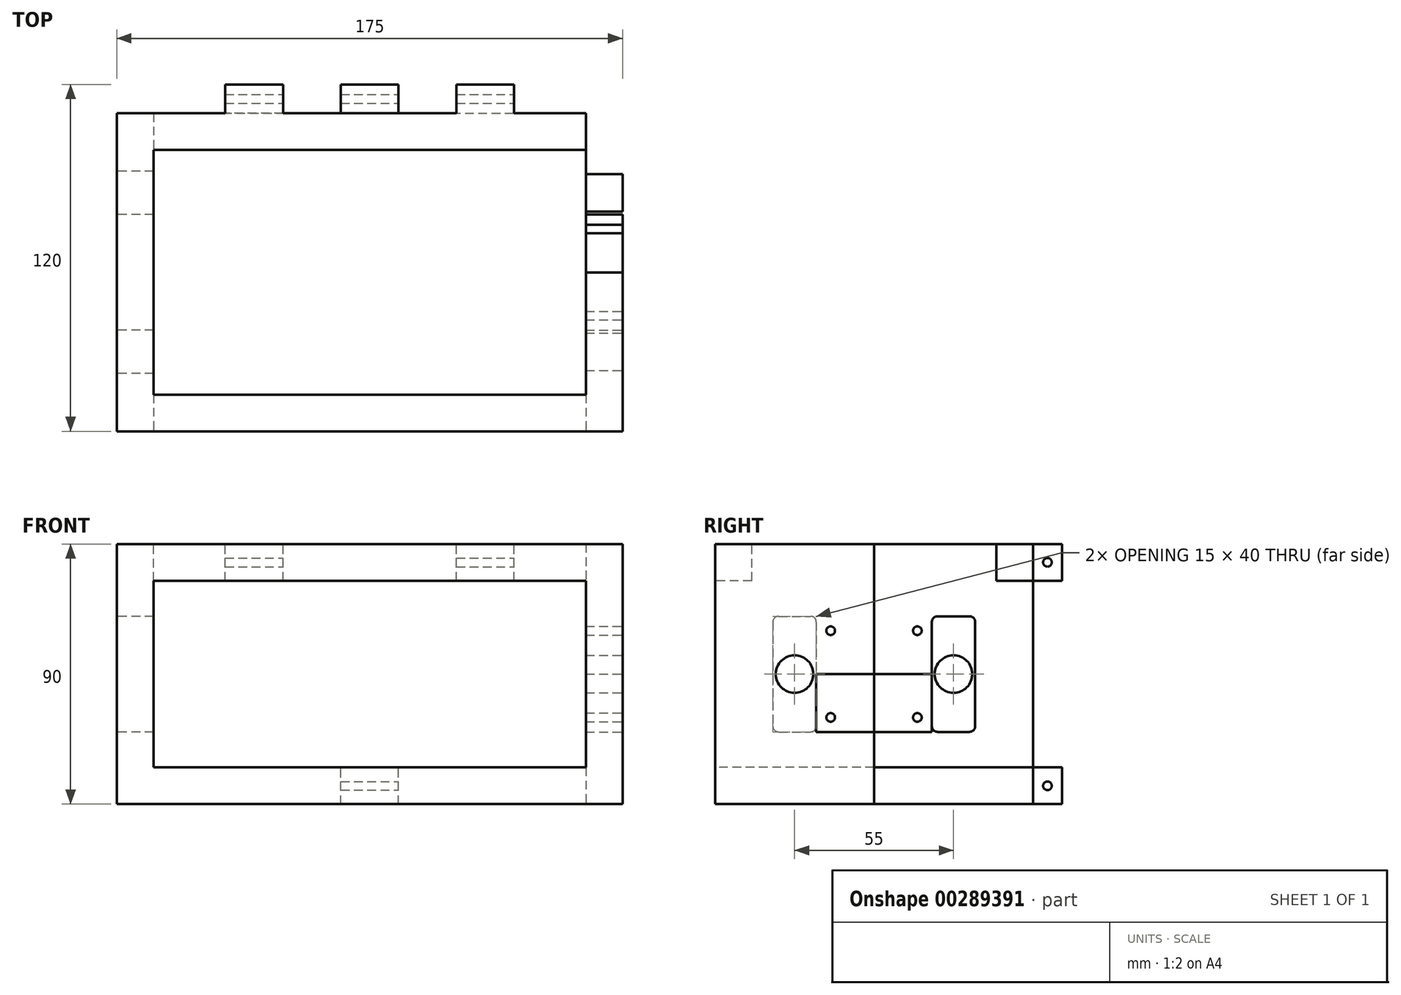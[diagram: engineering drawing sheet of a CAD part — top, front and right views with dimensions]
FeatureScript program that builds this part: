
annotation { "Feature Type Name" : "Feature", "Feature Type Description" : "" }
export const myFeature = defineFeature(function(context is Context, id is Id, definition is map)
    precondition{}
    {
        {
            var Q0;
            Q0=qCreatedBy(makeId("Front.planeOp"),FACE);
            var sketch = newSketch(context, id + "F0", { "sketchPlane" : qUnion([Q0])});
            skLineSegment(sketch, "E0.bottom", {"start": v(-87.5, 45) * mm, "end": v(87.5, 45) * mm});
            skLineSegment(sketch, "E0.top", {"start": v(-87.5, -45) * mm, "end": v(87.5, -45) * mm});
            skLineSegment(sketch, "E0.left", {"start": v(-87.5, 45) * mm, "end": v(-87.5, -45) * mm});
            skLineSegment(sketch, "E0.right", {"start": v(87.5, 45) * mm, "end": v(87.5, -45) * mm});
            skPoint(sketch, "E0.middle", {"position": v(0, 0) * mm});
            skSolve(sketch);
        }
        {
            var Q0;
            Q0 = qSketchRegion(id + "F0", true);
            extrude(context, id + "F1", {"entities" : qUnion([Q0]), "endBound" : BoundingType.SYMMETRIC, "depth" : 110 * mm});
        }
        {
            var Q0;
            Q0=makeQuery(id+"F1.opExtrude","SWEPT_FACE",FACE,{"disambiguationData":[OSD([sQuery(id+"F0.wireOp",EDGE,"E0.left")])]});
            var sketch = newSketch(context, id + "F2", { "sketchPlane" : qUnion([Q0])});
            skLineSegment(sketch, "E1", {"start": v(0, 45) * mm, "end": v(0, 10) * mm});
            skLineSegment(sketch, "E2", {"start": v(-55, 0) * mm, "end": v(-35, 0) * mm});
            skLineSegment(sketch, "E3.bottom", {"start": v(-33, 20) * mm, "end": v(-22, 20) * mm});
            skLineSegment(sketch, "E3.top", {"start": v(-33, -20) * mm, "end": v(-22, -20) * mm});
            skLineSegment(sketch, "E3.left", {"start": v(-35, 18) * mm, "end": v(-35, -18) * mm});
            skLineSegment(sketch, "E3.right", {"start": v(-20, 18) * mm, "end": v(-20, -18) * mm});
            skPoint(sketch, "E3.middle", {"position": v(-27.5, 0) * mm});
            skLineSegment(sketch, "E4.MirrorCS", {"start": v(20, 18) * mm, "end": v(20, -18) * mm});
            skLineSegment(sketch, "E5.MirrorCS", {"start": v(33, 20) * mm, "end": v(22, 20) * mm});
            skLineSegment(sketch, "E6.MirrorCS", {"start": v(35, 18) * mm, "end": v(35, -18) * mm});
            skLineSegment(sketch, "E7.MirrorCS", {"start": v(33, -20) * mm, "end": v(22, -20) * mm});
            skPoint(sketch, "E8.visualSharp", {"position": v(-35, 20) * mm});
            skArc(sketch, "E8.filletArc", {"start": v(-33, 20) * mm, "mid": v(-34.41, 19.41) * mm, "end": v(-35, 18) * mm});
            skPoint(sketch, "E9.visualSharp", {"position": v(-20, 20) * mm});
            skArc(sketch, "E9.filletArc", {"start": v(-20, 18) * mm, "mid": v(-20.59, 19.41) * mm, "end": v(-22, 20) * mm});
            skPoint(sketch, "E10.visualSharp", {"position": v(-35, -20) * mm});
            skArc(sketch, "E10.filletArc", {"start": v(-35, -18) * mm, "mid": v(-34.41, -19.41) * mm, "end": v(-33, -20) * mm});
            skPoint(sketch, "E11.visualSharp", {"position": v(-20, -20) * mm});
            skArc(sketch, "E11.filletArc", {"start": v(-22, -20) * mm, "mid": v(-20.59, -19.41) * mm, "end": v(-20, -18) * mm});
            skPoint(sketch, "E12.visualSharp", {"position": v(20, 20) * mm});
            skArc(sketch, "E12.filletArc", {"start": v(22, 20) * mm, "mid": v(20.59, 19.41) * mm, "end": v(20, 18) * mm});
            skPoint(sketch, "E13.visualSharp", {"position": v(35, 20) * mm});
            skArc(sketch, "E13.filletArc", {"start": v(35, 18) * mm, "mid": v(34.41, 19.41) * mm, "end": v(33, 20) * mm});
            skPoint(sketch, "E14.visualSharp", {"position": v(20, -20) * mm});
            skArc(sketch, "E14.filletArc", {"start": v(20, -18) * mm, "mid": v(20.59, -19.41) * mm, "end": v(22, -20) * mm});
            skPoint(sketch, "E15.visualSharp", {"position": v(35, -20) * mm});
            skArc(sketch, "E15.filletArc", {"start": v(33, -20) * mm, "mid": v(34.41, -19.41) * mm, "end": v(35, -18) * mm});
            skLineSegment(sketch, "E16.trimOffspring", {"start": v(-20, 0) * mm, "end": v(-2.5, 0) * mm});
            skLineSegment(sketch, "E17.trimOffspring", {"start": v(2.5, 0) * mm, "end": v(20, 0) * mm});
            skLineSegment(sketch, "E18.trimOffspring", {"start": v(0, -10) * mm, "end": v(0, -45) * mm});
            skLineSegment(sketch, "E19.trimOffspring", {"start": v(35, 0) * mm, "end": v(55, 0) * mm});
            skLineSegment(sketch, "E20", {"start": v(0, 10) * mm, "end": v(0, -10) * mm});
            skLineSegment(sketch, "E21", {"start": v(2.5, 0) * mm, "end": v(-2.5, 0) * mm});
            skSolve(sketch);
        }
        {
            var Q0;
            Q0=makeQuery(id+"F1.opExtrude","CAP_FACE",FACE,{"disambiguationData":[OSD([sQuery(id+"F0.wireOp",EDGE,"E0.bottom"),sQuery(id+"F0.wireOp",EDGE,"E0.top"),sQuery(id+"F0.wireOp",EDGE,"E0.left"),sQuery(id+"F0.wireOp",EDGE,"E0.right")])],"isStart":false});
            var sketch = newSketch(context, id + "F3", { "sketchPlane" : qUnion([Q0])});
            skLineSegment(sketch, "E22.bottom", {"start": v(74.8, -32.3) * mm, "end": v(-74.8, -32.3) * mm});
            skLineSegment(sketch, "E22.top", {"start": v(74.8, 32.3) * mm, "end": v(-74.8, 32.3) * mm});
            skLineSegment(sketch, "E22.left", {"start": v(74.8, -32.3) * mm, "end": v(74.8, 32.3) * mm});
            skLineSegment(sketch, "E22.right", {"start": v(-74.8, -32.3) * mm, "end": v(-74.8, 32.3) * mm});
            skPoint(sketch, "E22.middle", {"position": v(0, 0) * mm});
            skSolve(sketch);
        }
        {
            var Q0;
            Q0 = qSketchRegion(id + "F3", true);
            extrude(context, id + "F4", {"entities" : qUnion([Q0]), "operationType" : NewBodyOperationType.REMOVE, "oppositeDirection" : true, "depth" : 110 * mm});
        }
        {
            var Q0;
            Q0=makeQuery(id+"F1.opExtrude","SWEPT_FACE",FACE,{"disambiguationData":[OSD([sQuery(id+"F0.wireOp",EDGE,"E0.bottom")])]});
            var sketch = newSketch(context, id + "F5", { "sketchPlane" : qUnion([Q0])});
            skLineSegment(sketch, "E23.bottom", {"start": v(74.8, 42.3) * mm, "end": v(-74.8, 42.3) * mm});
            skLineSegment(sketch, "E23.top", {"start": v(74.8, -42.3) * mm, "end": v(-74.8, -42.3) * mm});
            skLineSegment(sketch, "E23.left", {"start": v(74.8, 42.3) * mm, "end": v(74.8, -42.3) * mm});
            skLineSegment(sketch, "E23.right", {"start": v(-74.8, 42.3) * mm, "end": v(-74.8, -42.3) * mm});
            skPoint(sketch, "E23.middle", {"position": v(0, 0) * mm});
            skSolve(sketch);
        }
        {
            var Q0;
            Q0 = qSketchRegion(id + "F5", true);
            extrude(context, id + "F6", {"entities" : qUnion([Q0]), "operationType" : NewBodyOperationType.REMOVE, "oppositeDirection" : true, "depth" : 12.7 * mm});
        }
        {
            var Q0;
            Q0 = qSketchRegion(id + "F2", true);
            extrude(context, id + "F7", {"entities" : qUnion([Q0]), "operationType" : NewBodyOperationType.REMOVE, "oppositeDirection" : true, "depth" : 12.7 * mm});
        }
        {
            var Q0;
            Q0=makeQuery(id+"F1.opExtrude","SWEPT_FACE",FACE,{"disambiguationData":[OSD([sQuery(id+"F0.wireOp",EDGE,"E0.right")])]});
            var sketch = newSketch(context, id + "F8", { "sketchPlane" : qUnion([Q0])});
            skCircle(sketch, "E24", {"center": v(-27.5, 0) * mm, "radius": 6.5 * mm});
            skLineSegment(sketch, "E25", {"start": v(0, 45) * mm, "end": v(0, -45) * mm});
            skCircle(sketch, "E26.MirrorC", {"center": v(27.5, 0) * mm, "radius": 6.5 * mm});
            skLineSegment(sketch, "E27", {"start": v(-55, 0) * mm, "end": v(55, 0) * mm});
            skCircle(sketch, "E28", {"center": v(-15, 15) * mm, "radius": 1.5 * mm});
            skLineSegment(sketch, "E29.bottom", {"start": v(-20, 20) * mm, "end": v(20, 20) * mm});
            skLineSegment(sketch, "E29.top", {"start": v(-20, -20) * mm, "end": v(20, -20) * mm});
            skLineSegment(sketch, "E29.left", {"start": v(-20, 20) * mm, "end": v(-20, -20) * mm});
            skLineSegment(sketch, "E29.right", {"start": v(20, 20) * mm, "end": v(20, -20) * mm});
            skPoint(sketch, "E29.middle", {"position": v(0, 0) * mm});
            skCircle(sketch, "E30.MirrorC", {"center": v(15, 15) * mm, "radius": 1.5 * mm});
            skCircle(sketch, "E31.MirrorC", {"center": v(15, -15) * mm, "radius": 1.5 * mm});
            skCircle(sketch, "E32.MirrorC", {"center": v(-15, -15) * mm, "radius": 1.5 * mm});
            skSolve(sketch);
        }
        {
            var Q0;
            {var subQ0=sQuery(id+"F8.wireOp",EDGE,"E27");var subQ1=sQuery(id+"F8.wireOp",EDGE,"E24");var subQ2=makeQuery(id+"F8.imprint","INTERSECT",VERTEX,{"disambiguationData":[OD(0.0)],"derivedFrom":[subQ1,subQ0]});Q0=makeQuery(id+"F8.imprint","IMPRINT",FACE,{"disambiguationData":[TD([[makeQuery(id+"F8.imprint","IMPRINT",EDGE,{"disambiguationData":[TD([[subQ2,1.0]])],"derivedFrom":subQ1}),1.0]])]});}
            var Q1;
            {var subQ0=sQuery(id+"F8.wireOp",EDGE,"E27");var subQ1=sQuery(id+"F8.wireOp",EDGE,"E24");var subQ2=makeQuery(id+"F8.imprint","INTERSECT",VERTEX,{"disambiguationData":[OD(0.0)],"derivedFrom":[subQ1,subQ0]});Q1=makeQuery(id+"F8.imprint","IMPRINT",FACE,{"disambiguationData":[TD([[makeQuery(id+"F8.imprint","IMPRINT",EDGE,{"disambiguationData":[TD([[subQ2,-1.0]])],"derivedFrom":subQ1}),1.0]])]});}
            var Q2;
            {var subQ0=sQuery(id+"F8.wireOp",EDGE,"E27");var subQ1=sQuery(id+"F8.wireOp",EDGE,"E26.MirrorC");var subQ2=makeQuery(id+"F8.imprint","INTERSECT",VERTEX,{"disambiguationData":[OD(0.0)],"derivedFrom":[subQ1,subQ0]});Q2=makeQuery(id+"F8.imprint","IMPRINT",FACE,{"disambiguationData":[TD([[makeQuery(id+"F8.imprint","IMPRINT",EDGE,{"disambiguationData":[TD([[subQ2,-1.0]])],"derivedFrom":subQ1}),-1.0]])]});}
            var Q3;
            {var subQ0=sQuery(id+"F8.wireOp",EDGE,"E27");var subQ1=sQuery(id+"F8.wireOp",EDGE,"E26.MirrorC");var subQ2=makeQuery(id+"F8.imprint","INTERSECT",VERTEX,{"disambiguationData":[OD(0.0)],"derivedFrom":[subQ1,subQ0]});Q3=makeQuery(id+"F8.imprint","IMPRINT",FACE,{"disambiguationData":[TD([[makeQuery(id+"F8.imprint","IMPRINT",EDGE,{"disambiguationData":[TD([[subQ2,1.0]])],"derivedFrom":subQ1}),-1.0]])]});}
            var Q4;
            Q4=makeQuery(id+"F8.imprint","IMPRINT",FACE,{"disambiguationData":[TD([[makeQuery(id+"F8.imprint","IMPRINT",EDGE,{"derivedFrom":sQuery(id+"F8.wireOp",EDGE,"E32.MirrorC")}),-1.0]])]});
            var Q5;
            Q5=makeQuery(id+"F8.imprint","IMPRINT",FACE,{"disambiguationData":[TD([[makeQuery(id+"F8.imprint","IMPRINT",EDGE,{"derivedFrom":sQuery(id+"F8.wireOp",EDGE,"E28")}),1.0]])]});
            var Q6;
            Q6=makeQuery(id+"F8.imprint","IMPRINT",FACE,{"disambiguationData":[TD([[makeQuery(id+"F8.imprint","IMPRINT",EDGE,{"derivedFrom":sQuery(id+"F8.wireOp",EDGE,"E30.MirrorC")}),-1.0]])]});
            var Q7;
            Q7=makeQuery(id+"F8.imprint","IMPRINT",FACE,{"disambiguationData":[TD([[makeQuery(id+"F8.imprint","IMPRINT",EDGE,{"derivedFrom":sQuery(id+"F8.wireOp",EDGE,"E31.MirrorC")}),1.0]])]});
            extrude(context, id + "F9", {"entities" : qUnion([Q0, Q1, Q2, Q3, Q4, Q5, Q6, Q7]), "operationType" : NewBodyOperationType.REMOVE, "oppositeDirection" : true, "depth" : 12.7 * mm});
        }
        {
            var Q0;
            Q0=makeQuery(id+"F1.opExtrude","CAP_FACE",FACE,{"disambiguationData":[OSD([sQuery(id+"F0.wireOp",EDGE,"E0.bottom"),sQuery(id+"F0.wireOp",EDGE,"E0.top"),sQuery(id+"F0.wireOp",EDGE,"E0.left"),sQuery(id+"F0.wireOp",EDGE,"E0.right")])],"isStart":true});
            var sketch = newSketch(context, id + "F10", { "sketchPlane" : qUnion([Q0])});
            skLineSegment(sketch, "E33", {"start": v(0, 45) * mm, "end": v(0, -45) * mm});
            skLineSegment(sketch, "E34.bottom", {"start": v(-10, -45) * mm, "end": v(10, -45) * mm});
            skLineSegment(sketch, "E34.top", {"start": v(-10, -32.3) * mm, "end": v(10, -32.3) * mm});
            skLineSegment(sketch, "E34.left", {"start": v(-10, -45) * mm, "end": v(-10, -32.3) * mm});
            skLineSegment(sketch, "E34.right", {"start": v(10, -45) * mm, "end": v(10, -32.3) * mm});
            skLineSegment(sketch, "E35.bottom", {"start": v(-30, 32.3) * mm, "end": v(-50, 32.3) * mm});
            skLineSegment(sketch, "E35.top", {"start": v(-30, 45) * mm, "end": v(-50, 45) * mm});
            skLineSegment(sketch, "E35.left", {"start": v(-30, 32.3) * mm, "end": v(-30, 45) * mm});
            skLineSegment(sketch, "E35.right", {"start": v(-50, 32.3) * mm, "end": v(-50, 45) * mm});
            skLineSegment(sketch, "E36.bottom", {"start": v(30, 32.3) * mm, "end": v(50, 32.3) * mm});
            skLineSegment(sketch, "E36.top", {"start": v(30, 45) * mm, "end": v(50, 45) * mm});
            skLineSegment(sketch, "E36.left", {"start": v(30, 32.3) * mm, "end": v(30, 45) * mm});
            skLineSegment(sketch, "E36.right", {"start": v(50, 32.3) * mm, "end": v(50, 45) * mm});
            skSolve(sketch);
        }
        {
            var Q0;
            Q0 = qSketchRegion(id + "F10", true);
            extrude(context, id + "F11", {"entities" : qUnion([Q0]), "operationType" : NewBodyOperationType.ADD, "depth" : 10 * mm});
        }
        {
            var Q0;
            Q0=makeQuery(id+"F11.opExtrude","SWEPT_FACE",FACE,{"disambiguationData":[OSD([sQuery(id+"F10.wireOp",EDGE,"E35.right")])]});
            var sketch = newSketch(context, id + "F12", { "sketchPlane" : qUnion([Q0])});
            skLineSegment(sketch, "E37", {"start": v(55, 45) * mm, "end": v(65, 32.3) * mm});
            skLineSegment(sketch, "E38", {"start": v(65, 45) * mm, "end": v(55, 32.3) * mm});
            skCircle(sketch, "E39", {"center": v(60, 38.65) * mm, "radius": 1.5 * mm});
            skSolve(sketch);
        }
        {
            var Q0;
            Q0 = qSketchRegion(id + "F12", true);
            extrude(context, id + "F13", {"entities" : qUnion([Q0]), "operationType" : NewBodyOperationType.REMOVE, "endBound" : BoundingType.THROUGH_ALL, "oppositeDirection" : true, "depth" : 25 * mm});
        }
        {
            var Q0;
            Q0=makeQuery(id+"F11.opExtrude","SWEPT_FACE",FACE,{"disambiguationData":[OSD([sQuery(id+"F10.wireOp",EDGE,"E34.left")])]});
            var sketch = newSketch(context, id + "F14", { "sketchPlane" : qUnion([Q0])});
            skLineSegment(sketch, "E40", {"start": v(55, -32.3) * mm, "end": v(65, -45) * mm});
            skLineSegment(sketch, "E41", {"start": v(65, -32.3) * mm, "end": v(55, -45) * mm});
            skCircle(sketch, "E42", {"center": v(60, -38.65) * mm, "radius": 1.5 * mm});
            skSolve(sketch);
        }
        {
            var Q0;
            Q0 = qSketchRegion(id + "F14", true);
            extrude(context, id + "F15", {"entities" : qUnion([Q0]), "operationType" : NewBodyOperationType.REMOVE, "endBound" : BoundingType.THROUGH_ALL, "oppositeDirection" : true, "depth" : 25 * mm});
        }
    });
